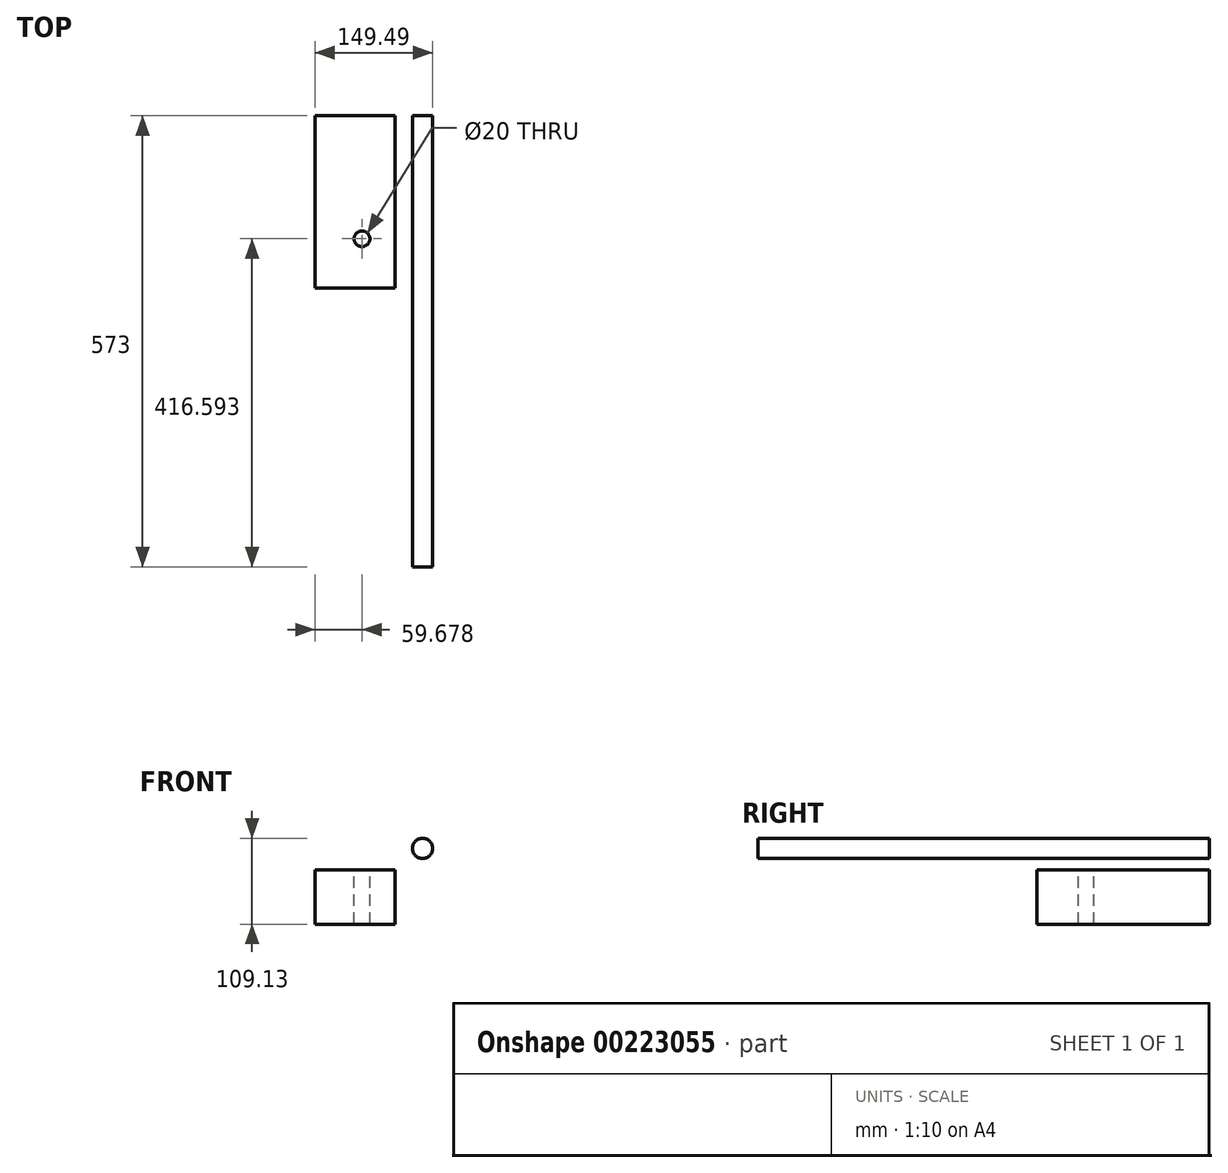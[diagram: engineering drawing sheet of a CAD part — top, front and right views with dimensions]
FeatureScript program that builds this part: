
annotation { "Feature Type Name" : "Feature", "Feature Type Description" : "" }
export const myFeature = defineFeature(function(context is Context, id is Id, definition is map)
    precondition{}
    {
        {
            var Q0;
            Q0=qCreatedBy(makeId("Front.planeOp"),FACE);
            var sketch = newSketch(context, id + "F0", { "sketchPlane" : qUnion([Q0])});
            skLineSegment(sketch, "E0.bottom", {"start": v(-43.83, 34.32) * mm, "end": v(58, 34.32) * mm});
            skLineSegment(sketch, "E0.top", {"start": v(-43.83, -34.7) * mm, "end": v(58, -34.7) * mm});
            skLineSegment(sketch, "E0.left", {"start": v(-43.83, 34.32) * mm, "end": v(-43.83, -34.7) * mm});
            skLineSegment(sketch, "E0.right", {"start": v(58, 34.32) * mm, "end": v(58, -34.7) * mm});
            skSolve(sketch);
        }
        {
            var Q0;
            Q0=makeQuery(id+"F0.imprint","IMPRINT",FACE,{"disambiguationData":[TD([[makeQuery(id+"F0.imprint","IMPRINT",EDGE,{"derivedFrom":sQuery(id+"F0.wireOp",EDGE,"E0.bottom")}),-1.0]])]});
            extrude(context, id + "F1", {"entities" : qUnion([Q0]), "depth" : 219 * mm});
        }
        {
            var Q0;
            Q0=qCreatedBy(makeId("Front.planeOp"),FACE);
            var sketch = newSketch(context, id + "F2", { "sketchPlane" : qUnion([Q0])});
            skCircle(sketch, "E1", {"center": v(92.78, 61.56) * mm, "radius": 12.88 * mm});
            skSolve(sketch);
        }
        {
            var Q0;
            Q0 = qSketchRegion(id + "F2", true);
            extrude(context, id + "F3", {"entities" : qUnion([Q0]), "depth" : 573 * mm});
        }
        {
            var Q0;
            Q0=makeQuery(id+"F1.opExtrude","SWEPT_FACE",FACE,{"disambiguationData":[OSD([sQuery(id+"F0.wireOp",EDGE,"E0.bottom")])]});
            var sketch = newSketch(context, id + "F4", { "sketchPlane" : qUnion([Q0])});
            skCircle(sketch, "E2", {"center": v(15.85, -156.4) * mm, "radius": 10 * mm});
            skSolve(sketch);
        }
        {
            var Q0;
            Q0 = qSketchRegion(id + "F4", true);
            extrude(context, id + "F5", {"entities" : qUnion([Q0]), "operationType" : NewBodyOperationType.REMOVE, "endBound" : BoundingType.THROUGH_ALL, "oppositeDirection" : true, "depth" : 25 * mm});
        }
    });
